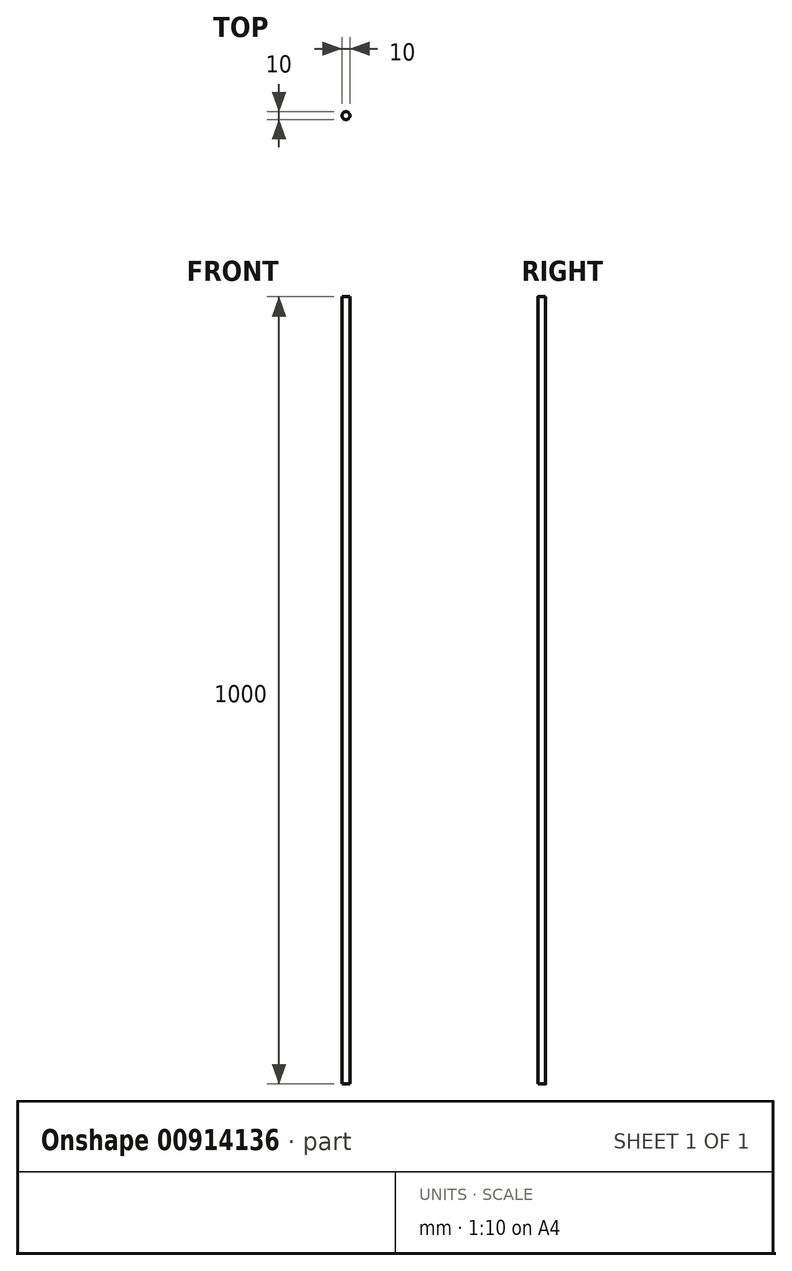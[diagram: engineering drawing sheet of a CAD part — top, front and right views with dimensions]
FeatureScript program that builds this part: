
annotation { "Feature Type Name" : "Feature", "Feature Type Description" : "" }
export const myFeature = defineFeature(function(context is Context, id is Id, definition is map)
    precondition{}
    {
        {
            var Q0;
            Q0=qCreatedBy(makeId("Top.planeOp"),FACE);
            var sketch = newSketch(context, id + "F0", { "sketchPlane" : qUnion([Q0])});
            skCircle(sketch, "E0", {"center": v(0, 0) * mm, "radius": 5 * mm});
            skSolve(sketch);
        }
        {
            var Q0;
            Q0=makeQuery(id+"F0.imprint","IMPRINT",FACE,{"disambiguationData":[TD([[makeQuery(id+"F0.imprint","IMPRINT",EDGE,{"derivedFrom":sQuery(id+"F0.wireOp",EDGE,"E0")}),1.0]])]});
            extrude(context, id + "F1", {"entities" : qUnion([Q0]), "depth" : 1000 * mm, "offsetDistance" : 25 * mm});
        }
    });
